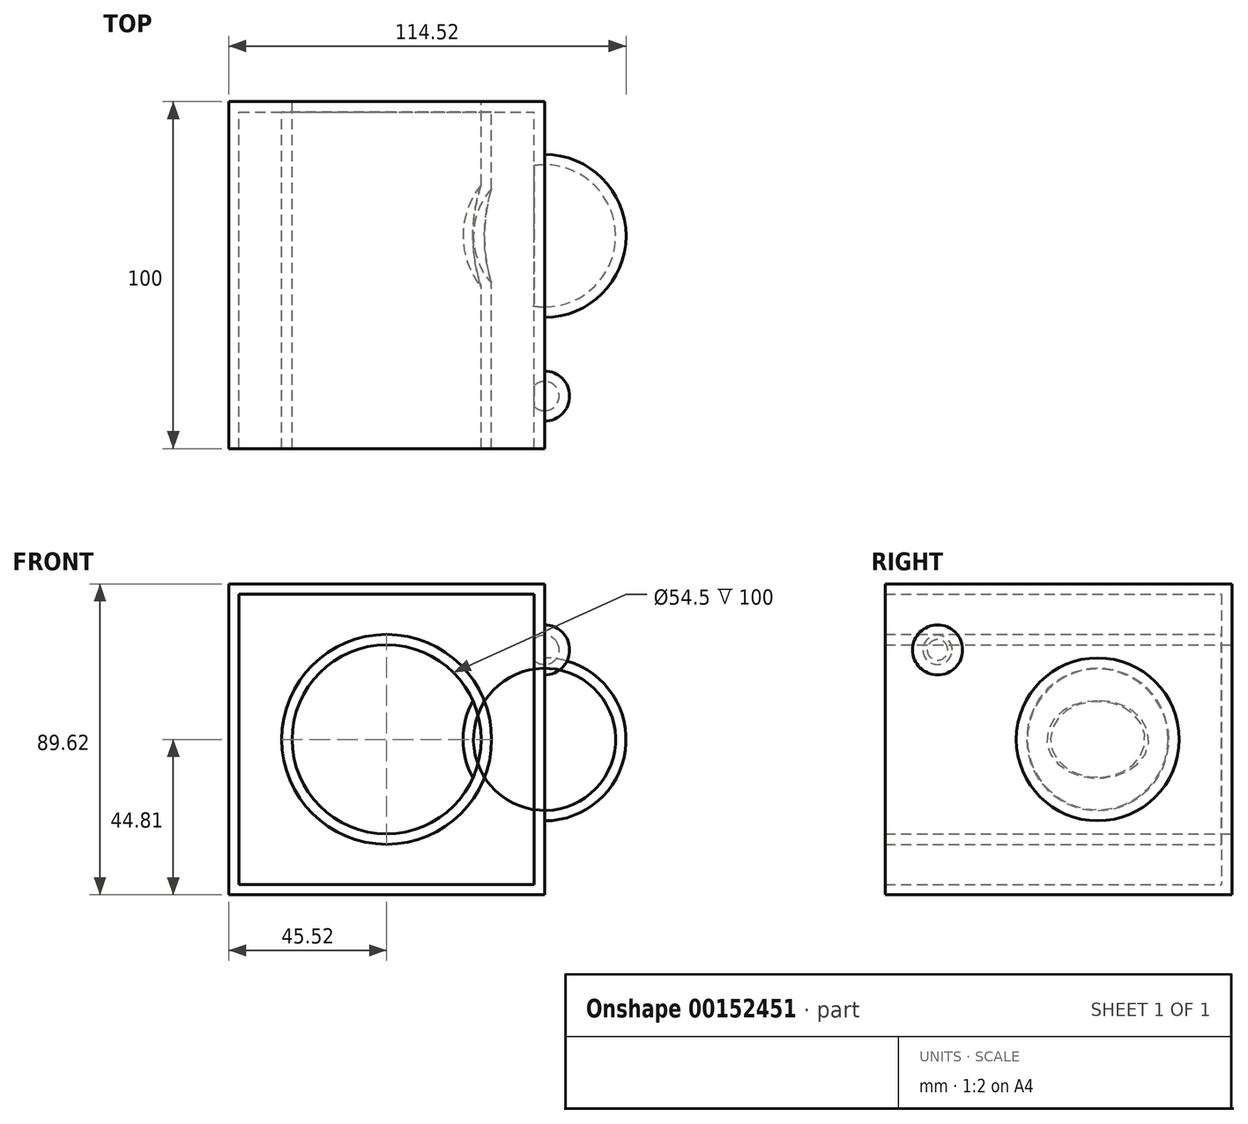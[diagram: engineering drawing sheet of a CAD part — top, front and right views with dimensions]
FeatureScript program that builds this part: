
annotation { "Feature Type Name" : "Feature", "Feature Type Description" : "" }
export const myFeature = defineFeature(function(context is Context, id is Id, definition is map)
    precondition{}
    {
        {
            var Q0;
            Q0=qCreatedBy(makeId("Front.planeOp"),FACE);
            var sketch = newSketch(context, id + "F0", { "sketchPlane" : qUnion([Q0])});
            skLineSegment(sketch, "E0.bottom", {"start": v(-45.52, 44.81) * mm, "end": v(45.52, 44.81) * mm});
            skLineSegment(sketch, "E0.top", {"start": v(-45.52, -44.81) * mm, "end": v(45.52, -44.81) * mm});
            skLineSegment(sketch, "E0.left", {"start": v(-45.52, 44.81) * mm, "end": v(-45.52, -44.81) * mm});
            skLineSegment(sketch, "E0.right", {"start": v(45.52, 44.81) * mm, "end": v(45.52, -44.81) * mm});
            skPoint(sketch, "E0.middle", {"position": v(0, 0) * mm});
            skCircle(sketch, "E1", {"center": v(0, 0) * mm, "radius": 27.25 * mm});
            skLineSegment(sketch, "E2.bottom", {"start": v(-45.52, 44.81) * mm, "end": v(-30.8, 44.81) * mm});
            skLineSegment(sketch, "E2.top", {"start": v(-45.52, 83.11) * mm, "end": v(-30.8, 83.11) * mm});
            skLineSegment(sketch, "E2.left", {"start": v(-45.52, 44.81) * mm, "end": v(-45.52, 83.11) * mm});
            skLineSegment(sketch, "E2.right", {"start": v(-30.8, 44.81) * mm, "end": v(-30.8, 83.11) * mm});
            skSolve(sketch);
        }
        {
            var Q0;
            Q0=makeQuery(id+"F0.imprint","IMPRINT",FACE,{"disambiguationData":[TD([[makeQuery(id+"F0.imprint","IMPRINT",EDGE,{"derivedFrom":sQuery(id+"F0.wireOp",EDGE,"E0.bottom")}),-1.0]])]});
            var Q1;
            Q1=makeQuery(id+"F0.imprint","IMPRINT",FACE,{"disambiguationData":[TD([[makeQuery(id+"F0.imprint","IMPRINT",EDGE,{"derivedFrom":sQuery(id+"F0.wireOp",EDGE,"E2.bottom")}),1.0]])]});
            extrude(context, id + "F1", {"entities" : qUnion([Q0, Q1]), "depth" : 100 * mm});
        }
        {
            var Q0;
            Q0=makeQuery(id+"F1.opExtrude","SWEPT_FACE",FACE,{"disambiguationData":[OSD([sQuery(id+"F0.wireOp",EDGE,"E0.right")])]});
            var sketch = newSketch(context, id + "F2", { "sketchPlane" : qUnion([Q0])});
            skCircle(sketch, "E3", {"center": v(-38.7, 0) * mm, "radius": 23.48 * mm});
            skLineSegment(sketch, "E4", {"start": v(-62.18, 0) * mm, "end": v(-15.22, 0) * mm});
            skCircle(sketch, "E5", {"center": v(-84.87, 25.79) * mm, "radius": 7.21 * mm});
            skLineSegment(sketch, "E6", {"start": v(-92.09, 25.79) * mm, "end": v(-77.66, 25.79) * mm});
            skSolve(sketch);
        }
        {
            var Q0;
            {var subQ0=sQuery(id+"F2.wireOp",EDGE,"E6");Q0=makeQuery(id+"F2.imprint","IMPRINT",FACE,{"disambiguationData":[TD([[makeQuery(id+"F2.imprint","IMPRINT",EDGE,{"derivedFrom":subQ0}),1.0]])]});}
            var Q1;
            Q1=sQuery(id+"F2.wireOp",EDGE,"E6");
            revolve(context, id + "F3", {"operationType" : NewBodyOperationType.ADD, "entities" : qUnion([Q0]), "axis" : qUnion([Q1]), "revolveType" : RevolveType.ONE_DIRECTION, "angle" : 180 * degree});
        }
        {
            var Q0;
            {var subQ0=sQuery(id+"F2.wireOp",EDGE,"E4");Q0=makeQuery(id+"F2.imprint","IMPRINT",FACE,{"disambiguationData":[TD([[makeQuery(id+"F2.imprint","IMPRINT",EDGE,{"derivedFrom":subQ0}),1.0]])]});}
            var Q1;
            Q1=sQuery(id+"F2.wireOp",EDGE,"E4");
            revolve(context, id + "F4", {"operationType" : NewBodyOperationType.ADD, "entities" : qUnion([Q0]), "axis" : qUnion([Q1]), "revolveType" : RevolveType.FULL});
        }
        {
            var Q0;
            Q0=makeQuery(id+"F1.opExtrude","CAP_FACE",FACE,{"disambiguationData":[OSD([sQuery(id+"F0.wireOp",EDGE,"E0.bottom"),sQuery(id+"F0.wireOp",EDGE,"E0.top"),sQuery(id+"F0.wireOp",EDGE,"E0.left"),sQuery(id+"F0.wireOp",EDGE,"E0.right"),sQuery(id+"F0.wireOp",EDGE,"E1"),sQuery(id+"F0.wireOp",EDGE,"E2.top"),sQuery(id+"F0.wireOp",EDGE,"E2.left"),sQuery(id+"F0.wireOp",EDGE,"E2.right")])],"isStart":false});
            shell(context, id + "F5", {"entities" : qUnion([Q0]), "thickness" : 3 * mm});
        }
    });
